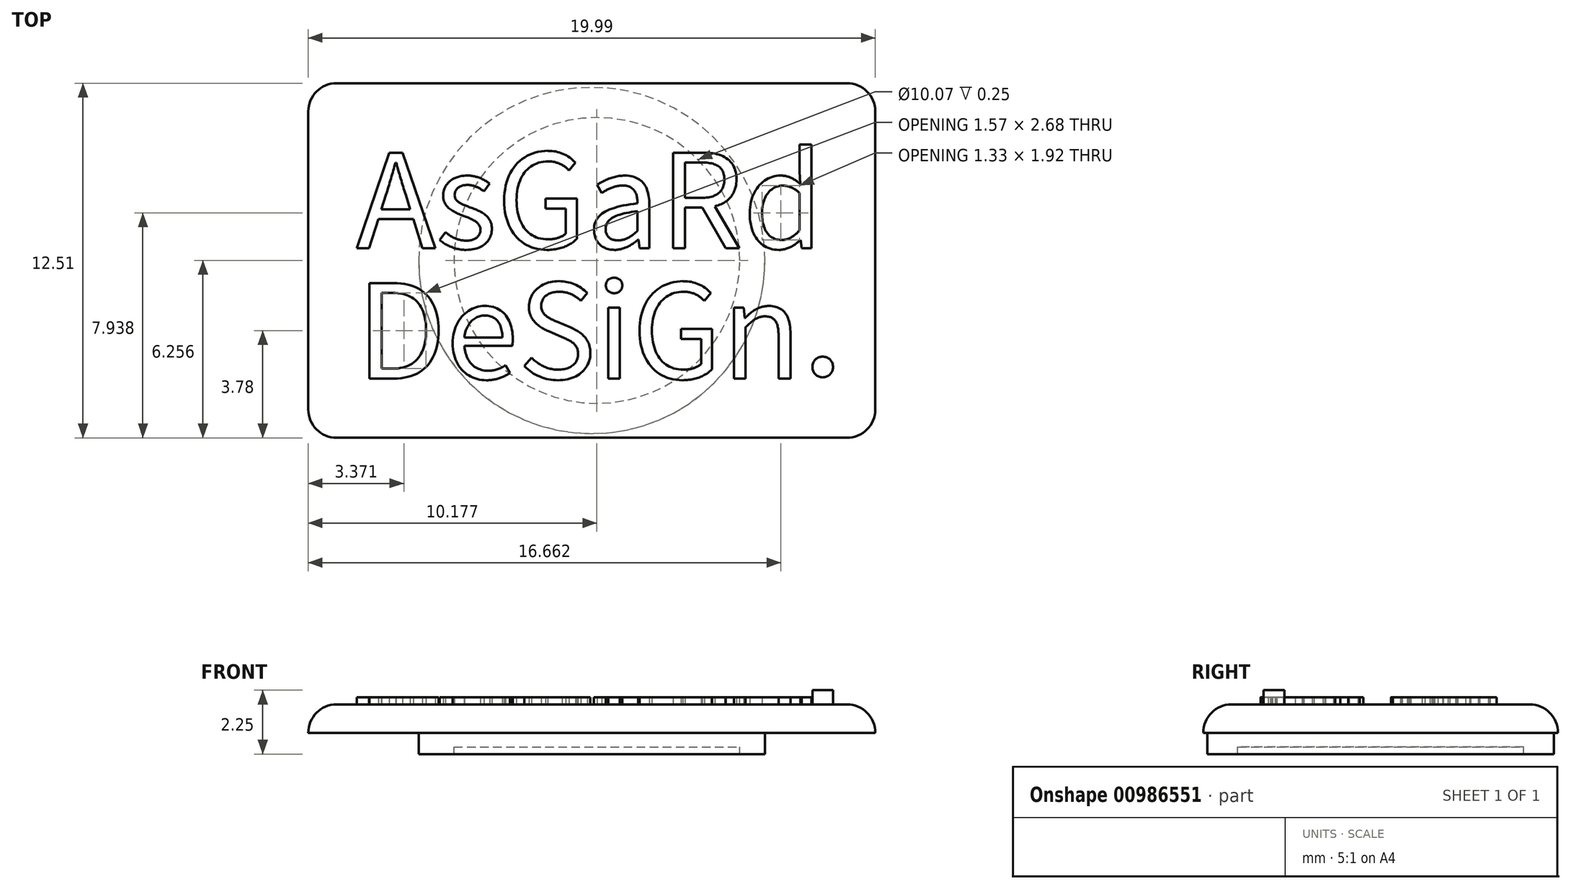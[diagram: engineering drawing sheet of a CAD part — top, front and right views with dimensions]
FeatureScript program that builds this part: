
annotation { "Feature Type Name" : "Feature", "Feature Type Description" : "" }
export const myFeature = defineFeature(function(context is Context, id is Id, definition is map)
    precondition{}
    {
        {
            var Q0;
            Q0=qCreatedBy(makeId("Top.planeOp"),FACE);
            var sketch = newSketch(context, id + "F0", { "sketchPlane" : qUnion([Q0])});
            skText(sketch, "E0", { "text": "AsGaRd\nDeSiGn", "fontName": "NotoSansCJKjp-Regular.otf"});
            const initialGuessF0  = {"E0": [-0.06057, -0.03018, 1, 0, 0.00331]};
            skSetInitialGuess(sketch, initialGuessF0);
            skSolve(sketch);
        }
        {
            var Q0;
            Q0=qSketchRegion(id+"F0",true);
            extrude(context, id + "F1", {"entities" : qUnion([Q0]), "depth" : 0.25 * mm, "offsetDistance" : 25.4 * mm});
        }
        {
            var Q0;
            Q0=qCreatedBy(makeId("Top.planeOp"),FACE);
            var sketch = newSketch(context, id + "F2", { "sketchPlane" : qUnion([Q0])});
            skLineSegment(sketch, "E1.bottom", {"start": v(-62.27, -24.36) * mm, "end": v(-42.28, -24.36) * mm});
            skLineSegment(sketch, "E1.top", {"start": v(-62.27, -36.87) * mm, "end": v(-42.28, -36.87) * mm});
            skLineSegment(sketch, "E1.left", {"start": v(-62.27, -24.36) * mm, "end": v(-62.27, -36.87) * mm});
            skLineSegment(sketch, "E1.right", {"start": v(-42.28, -24.36) * mm, "end": v(-42.28, -36.87) * mm});
            skSolve(sketch);
        }
        {
            var Q0;
            Q0=qSketchRegion(id+"F2",true);
            extrude(context, id + "F3", {"entities" : qUnion([Q0]), "oppositeDirection" : true, "depth" : 1 * mm, "offsetDistance" : 25 * mm});
        }
        {
            var Q0;
            Q0=makeQuery(id+"F3.opExtrude","CAP_FACE",FACE,{"disambiguationData":[OSD([sQuery(id+"F2.wireOp",EDGE,"E1.bottom"),sQuery(id+"F2.wireOp",EDGE,"E1.top"),sQuery(id+"F2.wireOp",EDGE,"E1.left"),sQuery(id+"F2.wireOp",EDGE,"E1.right")])],"isStart":true});
            var sketch = newSketch(context, id + "F4", { "sketchPlane" : qUnion([Q0])});
            skCircle(sketch, "E2", {"center": v(-44.13, -34.37) * mm, "radius": 0.37 * mm});
            skSolve(sketch);
        }
        {
            var Q0;
            Q0=makeQuery(id+"F4.imprint","IMPRINT",FACE,{"disambiguationData":[TD([[makeQuery(id+"F4.imprint","IMPRINT",EDGE,{"derivedFrom":sQuery(id+"F4.wireOp",EDGE,"E2")}),1.0]])]});
            extrude(context, id + "F5", {"entities" : qUnion([Q0]), "operationType" : NewBodyOperationType.ADD, "depth" : 0.5 * mm, "offsetDistance" : 25 * mm});
        }
        {
            var Q0;
            Q0=makeQuery(id+"F3.opExtrude","SWEPT_EDGE",EDGE,{"disambiguationData":[OSD([sQuery(id+"F2.wireOp",EDGE,"E1.top"),sQuery(id+"F2.wireOp",EDGE,"E1.left")])]});
            var Q1;
            Q1=makeQuery(id+"F3.opExtrude","SWEPT_EDGE",EDGE,{"disambiguationData":[OSD([sQuery(id+"F2.wireOp",EDGE,"E1.bottom"),sQuery(id+"F2.wireOp",EDGE,"E1.left")])]});
            var Q2;
            Q2=makeQuery(id+"F3.opExtrude","SWEPT_EDGE",EDGE,{"disambiguationData":[OSD([sQuery(id+"F2.wireOp",EDGE,"E1.top"),sQuery(id+"F2.wireOp",EDGE,"E1.right")])]});
            var Q3;
            Q3=makeQuery(id+"F3.opExtrude","SWEPT_EDGE",EDGE,{"disambiguationData":[OSD([sQuery(id+"F2.wireOp",EDGE,"E1.bottom"),sQuery(id+"F2.wireOp",EDGE,"E1.right")])]});
            fillet(context, id + "F6", {"entities" : qUnion([Q0, Q1, Q2, Q3]), "radius" : 1 * mm, "tangentPropagation" : true, "allowEdgeOverflow" : false});
        }
        {
            var Q0;
            {var subQ0=sQuery(id+"F2.wireOp",EDGE,"E1.left");var subQ1=sQuery(id+"F2.wireOp",EDGE,"E1.top");Q0=makeQuery(id+"F6.opFillet","BLEND_EDGE",EDGE,{"blendedFrom":[makeQuery(id+"F3.opExtrude","SWEPT_EDGE",EDGE,{"disambiguationData":[OSD([subQ1,subQ0])]}),makeQuery(id+"F3.opExtrude","CAP_FACE",FACE,{"disambiguationData":[OSD([sQuery(id+"F2.wireOp",EDGE,"E1.bottom"),subQ1,subQ0,sQuery(id+"F2.wireOp",EDGE,"E1.right")])],"isStart":true})],"blendedInto":[makeQuery(id+"F3.opExtrude","CAP_FACE",FACE,{"disambiguationData":[OSD([sQuery(id+"F2.wireOp",EDGE,"E1.bottom"),subQ1,subQ0,sQuery(id+"F2.wireOp",EDGE,"E1.right")])],"isStart":true})]});}
            fillet(context, id + "F7", {"entities" : qUnion([Q0]), "radius" : 1 * mm, "tangentPropagation" : true, "allowEdgeOverflow" : false});
        }
        {
            var Q0;
            Q0=makeQuery(id+"F3.opExtrude","CAP_FACE",FACE,{"disambiguationData":[OSD([sQuery(id+"F2.wireOp",EDGE,"E1.bottom"),sQuery(id+"F2.wireOp",EDGE,"E1.top"),sQuery(id+"F2.wireOp",EDGE,"E1.left"),sQuery(id+"F2.wireOp",EDGE,"E1.right")])],"isStart":false});
            var sketch = newSketch(context, id + "F8", { "sketchPlane" : qUnion([Q0])});
            skCircle(sketch, "E3", {"center": v(-52.27, 30.61) * mm, "radius": 6.1 * mm});
            skSolve(sketch);
        }
        {
            var Q0;
            Q0=makeQuery(id+"F8.imprint","IMPRINT",FACE,{"disambiguationData":[TD([[makeQuery(id+"F8.imprint","IMPRINT",EDGE,{"derivedFrom":sQuery(id+"F8.wireOp",EDGE,"E3")}),1.0]])]});
            extrude(context, id + "F9", {"entities" : qUnion([Q0]), "operationType" : NewBodyOperationType.ADD, "depth" : 0.5 * mm, "offsetDistance" : 25 * mm});
        }
        {
            var Q0;
            Q0=makeQuery(id+"F9.opExtrude","CAP_FACE",FACE,{"disambiguationData":[OSD([sQuery(id+"F8.wireOp",EDGE,"E3")])],"isStart":false});
            var sketch = newSketch(context, id + "F10", { "sketchPlane" : qUnion([Q0])});
            skCircle(sketch, "E4", {"center": v(-52.1, 30.61) * mm, "radius": 5.04 * mm});
            skSolve(sketch);
        }
        {
            var Q0;
            Q0=makeQuery(id+"F10.imprint","IMPRINT",FACE,{"disambiguationData":[TD([[makeQuery(id+"F10.imprint","IMPRINT",EDGE,{"derivedFrom":sQuery(id+"F10.wireOp",EDGE,"E4")}),-1.0]])]});
            extrude(context, id + "F11", {"entities" : qUnion([Q0]), "operationType" : NewBodyOperationType.ADD, "depth" : 0.25 * mm, "offsetDistance" : 25 * mm});
        }
    });
